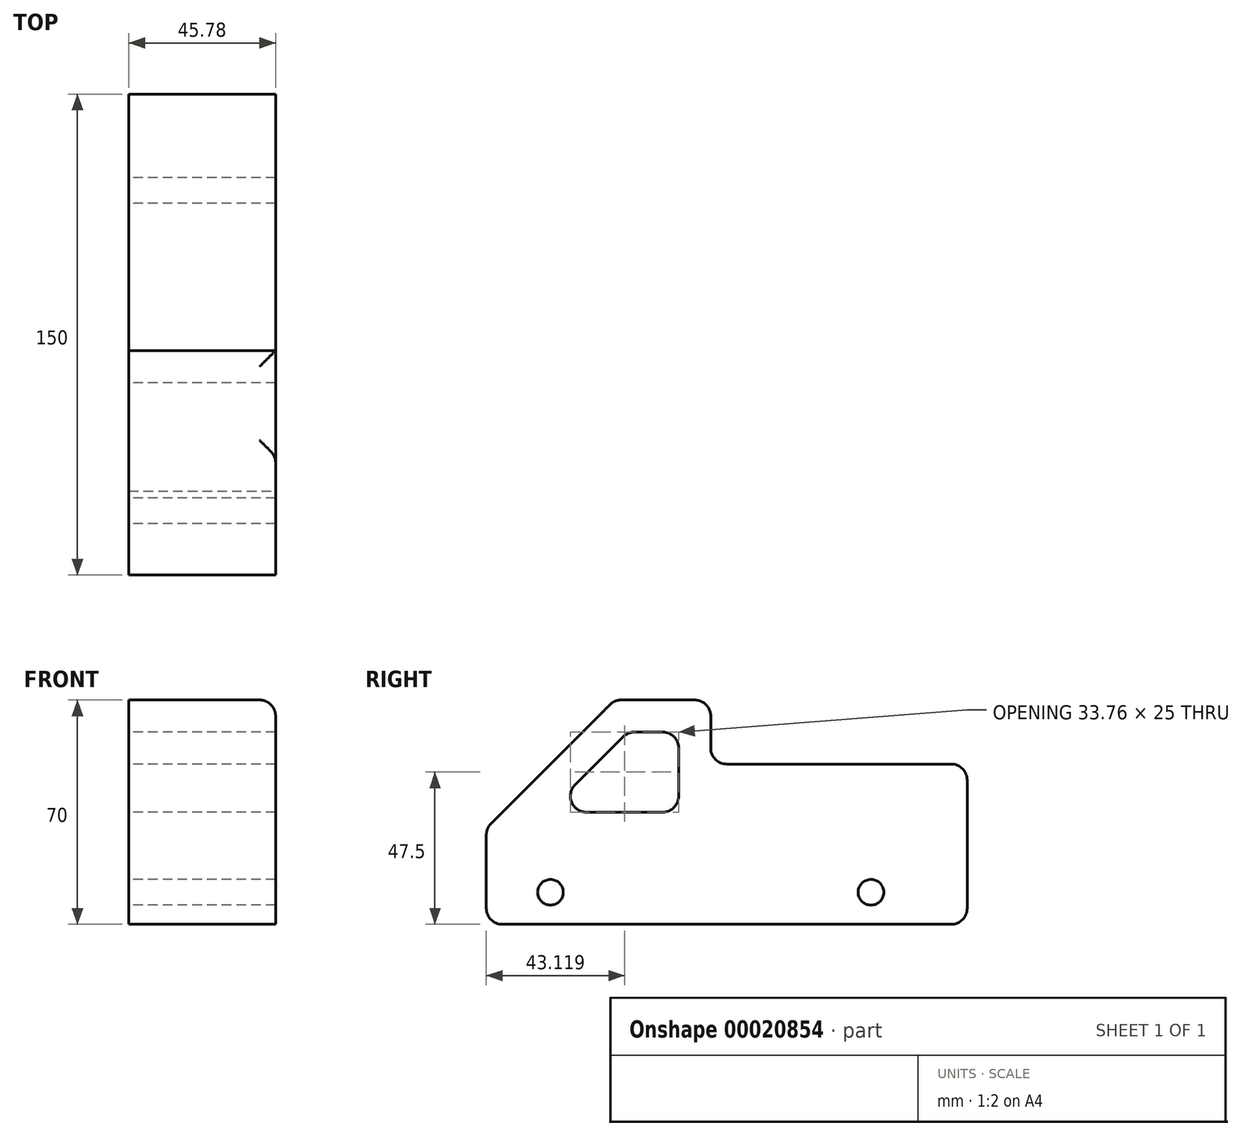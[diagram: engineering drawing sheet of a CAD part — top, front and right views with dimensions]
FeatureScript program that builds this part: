
annotation { "Feature Type Name" : "Feature", "Feature Type Description" : "" }
export const myFeature = defineFeature(function(context is Context, id is Id, definition is map)
    precondition{}
    {
        {
            var Q0;
            Q0=qCreatedBy(makeId("Right.planeOp"),FACE);
            var sketch = newSketch(context, id + "F0", { "sketchPlane" : qUnion([Q0])});
            skLineSegment(sketch, "E0", {"start": v(0, 0) * mm, "end": v(0, 30) * mm});
            skLineSegment(sketch, "E1", {"start": v(0, 30) * mm, "end": v(40, 70) * mm});
            skLineSegment(sketch, "E2", {"start": v(40, 70) * mm, "end": v(70, 70) * mm});
            skLineSegment(sketch, "E3", {"start": v(70, 70) * mm, "end": v(70, 50) * mm});
            skLineSegment(sketch, "E4", {"start": v(70, 50) * mm, "end": v(150, 50) * mm});
            skLineSegment(sketch, "E5", {"start": v(150, 50) * mm, "end": v(150, 0) * mm});
            skLineSegment(sketch, "E6", {"start": v(150, 0) * mm, "end": v(0, 0) * mm});
            skLineSegment(sketch, "E7.0", {"start": v(60, 60) * mm, "end": v(60, 35) * mm});
            skLineSegment(sketch, "E7.1", {"start": v(44.14, 60) * mm, "end": v(60, 60) * mm});
            skLineSegment(sketch, "E7.2", {"start": v(19.14, 35) * mm, "end": v(44.14, 60) * mm});
            skLineSegment(sketch, "E8", {"start": v(60, 35) * mm, "end": v(19.14, 35) * mm});
            skCircle(sketch, "E9", {"center": v(20, 10) * mm, "radius": 4 * mm});
            skCircle(sketch, "E10", {"center": v(120, 10) * mm, "radius": 4 * mm});
            skSolve(sketch);
        }
        {
            var Q0;
            Q0=makeQuery(id+"F0.imprint","IMPRINT",FACE,{"disambiguationData":[TD([[makeQuery(id+"F0.imprint","IMPRINT",EDGE,{"derivedFrom":sQuery(id+"F0.wireOp",EDGE,"E0")}),-1.0]])]});
            extrude(context, id + "F1", {"entities" : qUnion([Q0]), "depth" : 45.78 * mm});
        }
        {
            var Q0;
            Q0=makeQuery(id+"F1.opExtrude","SWEPT_EDGE",EDGE,{"disambiguationData":[OSD([sQuery(id+"F0.wireOp",EDGE,"E1"),sQuery(id+"F0.wireOp",EDGE,"E2")])]});
            var Q1;
            Q1=makeQuery(id+"F1.opExtrude","SWEPT_EDGE",EDGE,{"disambiguationData":[OSD([sQuery(id+"F0.wireOp",EDGE,"E2"),sQuery(id+"F0.wireOp",EDGE,"E3")])]});
            var Q2;
            Q2=makeQuery(id+"F1.opExtrude","CAP_EDGE",EDGE,{"disambiguationData":[OSD([sQuery(id+"F0.wireOp",EDGE,"E2")])],"isStart":false});
            var Q3;
            Q3=makeQuery(id+"F1.opExtrude","SWEPT_EDGE",EDGE,{"disambiguationData":[OSD([sQuery(id+"F0.wireOp",EDGE,"E7.2"),sQuery(id+"F0.wireOp",EDGE,"E8")])]});
            var Q4;
            Q4=makeQuery(id+"F1.opExtrude","SWEPT_EDGE",EDGE,{"disambiguationData":[OSD([sQuery(id+"F0.wireOp",EDGE,"E0"),sQuery(id+"F0.wireOp",EDGE,"E1")])]});
            var Q5;
            Q5=makeQuery(id+"F1.opExtrude","SWEPT_EDGE",EDGE,{"disambiguationData":[OSD([sQuery(id+"F0.wireOp",EDGE,"E0"),sQuery(id+"F0.wireOp",EDGE,"E6")])]});
            var Q6;
            Q6=makeQuery(id+"F1.opExtrude","SWEPT_EDGE",EDGE,{"disambiguationData":[OSD([sQuery(id+"F0.wireOp",EDGE,"E3"),sQuery(id+"F0.wireOp",EDGE,"E4")])]});
            var Q7;
            Q7=makeQuery(id+"F1.opExtrude","SWEPT_EDGE",EDGE,{"disambiguationData":[OSD([sQuery(id+"F0.wireOp",EDGE,"E4"),sQuery(id+"F0.wireOp",EDGE,"E5")])]});
            var Q8;
            Q8=makeQuery(id+"F1.opExtrude","SWEPT_EDGE",EDGE,{"disambiguationData":[OSD([sQuery(id+"F0.wireOp",EDGE,"E5"),sQuery(id+"F0.wireOp",EDGE,"E6")])]});
            var Q9;
            Q9=makeQuery(id+"F1.opExtrude","SWEPT_EDGE",EDGE,{"disambiguationData":[OSD([sQuery(id+"F0.wireOp",EDGE,"E7.1"),sQuery(id+"F0.wireOp",EDGE,"E7.2")])]});
            var Q10;
            Q10=makeQuery(id+"F1.opExtrude","SWEPT_EDGE",EDGE,{"disambiguationData":[OSD([sQuery(id+"F0.wireOp",EDGE,"E7.0"),sQuery(id+"F0.wireOp",EDGE,"E8")])]});
            var Q11;
            Q11=makeQuery(id+"F1.opExtrude","SWEPT_EDGE",EDGE,{"disambiguationData":[OSD([sQuery(id+"F0.wireOp",EDGE,"E7.0"),sQuery(id+"F0.wireOp",EDGE,"E7.1")])]});
            fillet(context, id + "F2", {"entities" : qUnion([Q0, Q1, Q2, Q3, Q4, Q5, Q6, Q7, Q8, Q9, Q10, Q11]), "radius" : 5 * mm, "tangentPropagation" : true, "allowEdgeOverflow" : false});
        }
    });
